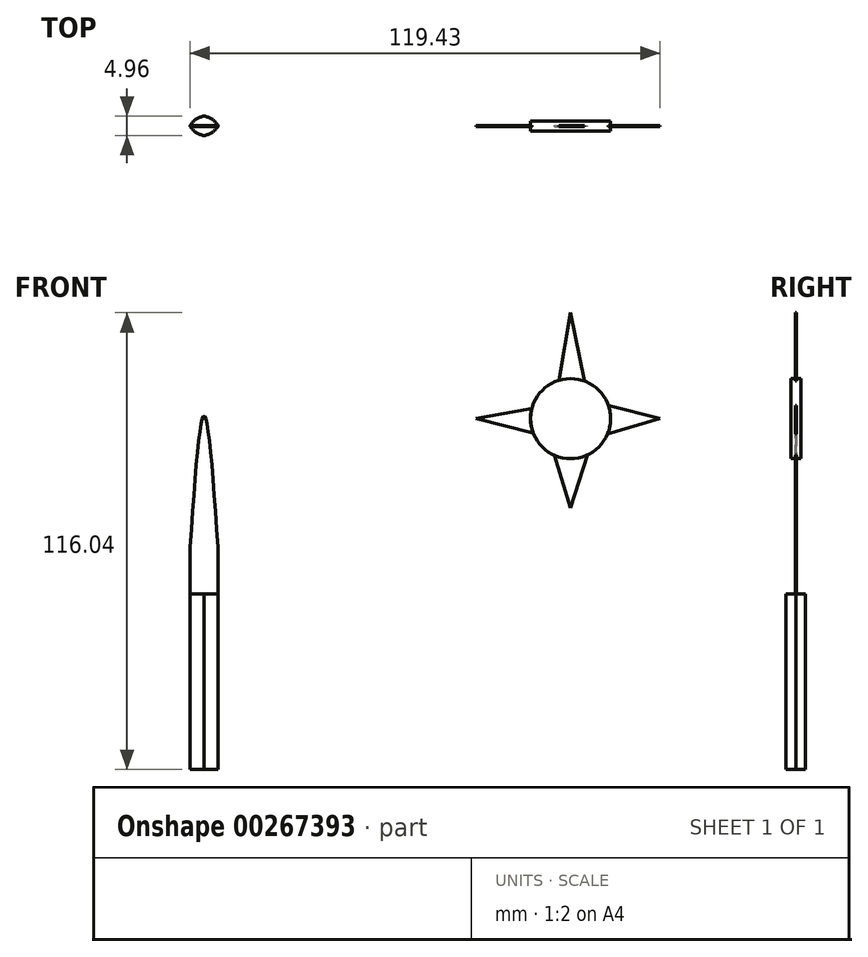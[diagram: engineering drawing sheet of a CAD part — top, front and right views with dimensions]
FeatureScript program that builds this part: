
annotation { "Feature Type Name" : "Feature", "Feature Type Description" : "" }
export const myFeature = defineFeature(function(context is Context, id is Id, definition is map)
    precondition{}
    {
        {
            var Q0;
            Q0=qCreatedBy(makeId("Front.planeOp"),FACE);
            var sketch = newSketch(context, id + "F0", { "sketchPlane" : qUnion([Q0])});
            skLineSegment(sketch, "E0.bottom", {"start": v(-61.66, -49.15) * mm, "end": v(-53.12, -49.15) * mm});
            skLineSegment(sketch, "E0.top", {"start": v(-61.66, -4.58) * mm, "end": v(-53.12, -4.58) * mm});
            skLineSegment(sketch, "E0.left", {"start": v(-61.66, -49.15) * mm, "end": v(-61.66, -4.58) * mm});
            skLineSegment(sketch, "E0.right", {"start": v(-53.12, -49.15) * mm, "end": v(-53.12, -4.58) * mm});
            skPoint(sketch, "E1.1.internal.snap0", {"position": v(-57.4, -4.58) * mm});
            skFitSpline(sketch, "E1", {"points": [v(-61.66, -4.58) * mm, v(-57.4, 40.6) * mm, v(-53.12, -4.58) * mm], "startDerivative": vector(8.55, 135.54) * mm, "endDerivative": vector(8.55, -135.54) * mm});
            skLineSegment(sketch, "E2", {"start": v(-61.66, -4.58) * mm, "end": v(-53.12, -8.83) * mm});
            skLineSegment(sketch, "E3", {"start": v(-53.12, -8.83) * mm, "end": v(-61.66, -12.87) * mm});
            skLineSegment(sketch, "E4", {"start": v(-61.66, -12.87) * mm, "end": v(-53.12, -15.68) * mm});
            skLineSegment(sketch, "E5", {"start": v(-53.12, -15.68) * mm, "end": v(-61.66, -19.7) * mm});
            skLineSegment(sketch, "E6", {"start": v(-61.66, -19.7) * mm, "end": v(-53.12, -23.53) * mm});
            skLineSegment(sketch, "E7", {"start": v(-53.12, -23.53) * mm, "end": v(-61.66, -27.49) * mm});
            skLineSegment(sketch, "E8", {"start": v(-61.66, -27.49) * mm, "end": v(-53.12, -31.45) * mm});
            skLineSegment(sketch, "E9", {"start": v(-53.12, -31.45) * mm, "end": v(-61.66, -37.05) * mm});
            skLineSegment(sketch, "E10", {"start": v(-61.66, -37.05) * mm, "end": v(-53.12, -41.01) * mm});
            skLineSegment(sketch, "E11", {"start": v(-53.12, -41.01) * mm, "end": v(-61.66, -44.67) * mm});
            skLineSegment(sketch, "E12", {"start": v(-61.66, -44.67) * mm, "end": v(-53.12, -49.15) * mm});
            skSolve(sketch);
        }
        {
            var Q0;
            Q0=makeQuery(id+"F0.imprint","IMPRINT",FACE,{"disambiguationData":[TD([[makeQuery(id+"F0.imprint","IMPRINT",EDGE,{"derivedFrom":sQuery(id+"F0.wireOp",EDGE,"E0.top")}),1.0]])]});
            extrude(context, id + "F1", {"entities" : qUnion([Q0]), "endBound" : BoundingType.SYMMETRIC, "depth" : 0.25 * mm});
        }
        {
            var Q0;
            {var subQ0=sQuery(id+"F0.wireOp",EDGE,"E0.top");Q0=makeQuery(id+"F0.imprint","IMPRINT",FACE,{"disambiguationData":[TD([[makeQuery(id+"F0.imprint","IMPRINT",EDGE,{"derivedFrom":subQ0}),-1.0]])]});}
            var Q1;
            {var subQ0=sQuery(id+"F0.wireOp",EDGE,"E2");Q1=makeQuery(id+"F0.imprint","IMPRINT",FACE,{"disambiguationData":[TD([[makeQuery(id+"F0.imprint","IMPRINT",EDGE,{"derivedFrom":subQ0}),-1.0]])]});}
            var Q2;
            {var subQ0=sQuery(id+"F0.wireOp",EDGE,"E3");Q2=makeQuery(id+"F0.imprint","IMPRINT",FACE,{"disambiguationData":[TD([[makeQuery(id+"F0.imprint","IMPRINT",EDGE,{"derivedFrom":subQ0}),1.0]])]});}
            var Q3;
            {var subQ0=sQuery(id+"F0.wireOp",EDGE,"E4");Q3=makeQuery(id+"F0.imprint","IMPRINT",FACE,{"disambiguationData":[TD([[makeQuery(id+"F0.imprint","IMPRINT",EDGE,{"derivedFrom":subQ0}),-1.0]])]});}
            var Q4;
            {var subQ0=sQuery(id+"F0.wireOp",EDGE,"E5");Q4=makeQuery(id+"F0.imprint","IMPRINT",FACE,{"disambiguationData":[TD([[makeQuery(id+"F0.imprint","IMPRINT",EDGE,{"derivedFrom":subQ0}),1.0]])]});}
            var Q5;
            {var subQ0=sQuery(id+"F0.wireOp",EDGE,"E6");Q5=makeQuery(id+"F0.imprint","IMPRINT",FACE,{"disambiguationData":[TD([[makeQuery(id+"F0.imprint","IMPRINT",EDGE,{"derivedFrom":subQ0}),-1.0]])]});}
            var Q6;
            {var subQ0=sQuery(id+"F0.wireOp",EDGE,"E7");Q6=makeQuery(id+"F0.imprint","IMPRINT",FACE,{"disambiguationData":[TD([[makeQuery(id+"F0.imprint","IMPRINT",EDGE,{"derivedFrom":subQ0}),1.0]])]});}
            var Q7;
            {var subQ0=sQuery(id+"F0.wireOp",EDGE,"E8");Q7=makeQuery(id+"F0.imprint","IMPRINT",FACE,{"disambiguationData":[TD([[makeQuery(id+"F0.imprint","IMPRINT",EDGE,{"derivedFrom":subQ0}),-1.0]])]});}
            var Q8;
            {var subQ0=sQuery(id+"F0.wireOp",EDGE,"E9");Q8=makeQuery(id+"F0.imprint","IMPRINT",FACE,{"disambiguationData":[TD([[makeQuery(id+"F0.imprint","IMPRINT",EDGE,{"derivedFrom":subQ0}),1.0]])]});}
            var Q9;
            {var subQ0=sQuery(id+"F0.wireOp",EDGE,"E10");Q9=makeQuery(id+"F0.imprint","IMPRINT",FACE,{"disambiguationData":[TD([[makeQuery(id+"F0.imprint","IMPRINT",EDGE,{"derivedFrom":subQ0}),-1.0]])]});}
            var Q10;
            {var subQ2=sQuery(id+"F0.wireOp",EDGE,"E11");Q10=makeQuery(id+"F0.imprint","IMPRINT",FACE,{"disambiguationData":[TD([[makeQuery(id+"F0.imprint","IMPRINT",EDGE,{"derivedFrom":subQ2}),1.0]])]});}
            var Q11;
            {var subQ0=sQuery(id+"F0.wireOp",EDGE,"E0.bottom");Q11=makeQuery(id+"F0.imprint","IMPRINT",FACE,{"disambiguationData":[TD([[makeQuery(id+"F0.imprint","IMPRINT",EDGE,{"derivedFrom":subQ0}),1.0]])]});}
            extrude(context, id + "F2", {"entities" : qUnion([Q0, Q1, Q2, Q3, Q4, Q5, Q6, Q7, Q8, Q9, Q10, Q11]), "operationType" : NewBodyOperationType.ADD, "endBound" : BoundingType.SYMMETRIC, "depth" : 5.08 * mm});
        }
        {
            var Q0;
            Q0=makeQuery(id+"F2.opExtrude","CAP_EDGE",EDGE,{"disambiguationData":[OSD([sQuery(id+"F0.wireOp",EDGE,"E0.left")])],"isStart":true});
            var Q1;
            Q1=makeQuery(id+"F2.opExtrude","CAP_EDGE",EDGE,{"disambiguationData":[OSD([sQuery(id+"F0.wireOp",EDGE,"E0.left")])],"isStart":false});
            var Q2;
            Q2=makeQuery(id+"F2.opExtrude","CAP_EDGE",EDGE,{"disambiguationData":[OSD([sQuery(id+"F0.wireOp",EDGE,"E0.right")])],"isStart":false});
            var Q3;
            Q3=makeQuery(id+"F2.opExtrude","CAP_EDGE",EDGE,{"disambiguationData":[OSD([sQuery(id+"F0.wireOp",EDGE,"E0.right")])],"isStart":true});
            fillet(context, id + "F3", {"entities" : qUnion([Q0, Q1, Q2, Q3]), "radius" : 5.08 * mm, "tangentPropagation" : true, "allowEdgeOverflow" : false});
        }
        {
            var Q0;
            Q0=qCreatedBy(makeId("Front.planeOp"),FACE);
            var sketch = newSketch(context, id + "F4", { "sketchPlane" : qUnion([Q0])});
            skCircle(sketch, "E13", {"center": v(35.72, 40) * mm, "radius": 10.17 * mm});
            skLineSegment(sketch, "E14", {"start": v(11.67, 40) * mm, "end": v(25.87, 42.54) * mm});
            skLineSegment(sketch, "E15", {"start": v(11.67, 40) * mm, "end": v(26.22, 36.35) * mm});
            skLineSegment(sketch, "E16", {"start": v(35.72, 17.32) * mm, "end": v(39.99, 30.77) * mm});
            skLineSegment(sketch, "E17", {"start": v(35.72, 17.32) * mm, "end": v(31.67, 30.66) * mm});
            skLineSegment(sketch, "E18", {"start": v(58.45, 40) * mm, "end": v(45.1, 36.09) * mm});
            skLineSegment(sketch, "E19", {"start": v(58.45, 40) * mm, "end": v(45.34, 43.26) * mm});
            skLineSegment(sketch, "E20", {"start": v(35.72, 66.89) * mm, "end": v(39.3, 49.5) * mm});
            skLineSegment(sketch, "E21", {"start": v(35.72, 66.89) * mm, "end": v(32.79, 49.72) * mm});
            skSolve(sketch);
        }
        {
            var Q0;
            {var subQ0=sQuery(id+"F4.wireOp",EDGE,"E13");var subQ5=makeQuery(id+"F4.imprint","INTERSECT",VERTEX,{"derivedFrom":[subQ0,sQuery(id+"F4.wireOp",EDGE,"E19")]});Q0=makeQuery(id+"F4.imprint","IMPRINT",FACE,{"disambiguationData":[TD([[makeQuery(id+"F4.imprint","IMPRINT",EDGE,{"disambiguationData":[TD([[subQ5,-1.0]])],"derivedFrom":subQ0}),1.0]])]});}
            extrude(context, id + "F5", {"entities" : qUnion([Q0]), "endBound" : BoundingType.SYMMETRIC, "depth" : 2.54 * mm});
        }
        {
            var Q0;
            {var subQ0=sQuery(id+"F4.wireOp",EDGE,"E14");Q0=makeQuery(id+"F4.imprint","IMPRINT",FACE,{"disambiguationData":[TD([[makeQuery(id+"F4.imprint","IMPRINT",EDGE,{"derivedFrom":subQ0}),-1.0]])]});}
            var Q1;
            {var subQ0=sQuery(id+"F4.wireOp",EDGE,"E20");Q1=makeQuery(id+"F4.imprint","IMPRINT",FACE,{"disambiguationData":[TD([[makeQuery(id+"F4.imprint","IMPRINT",EDGE,{"derivedFrom":subQ0}),-1.0]])]});}
            var Q2;
            {var subQ0=sQuery(id+"F4.wireOp",EDGE,"E16");Q2=makeQuery(id+"F4.imprint","IMPRINT",FACE,{"disambiguationData":[TD([[makeQuery(id+"F4.imprint","IMPRINT",EDGE,{"derivedFrom":subQ0}),1.0]])]});}
            var Q3;
            {var subQ0=sQuery(id+"F4.wireOp",EDGE,"E18");Q3=makeQuery(id+"F4.imprint","IMPRINT",FACE,{"disambiguationData":[TD([[makeQuery(id+"F4.imprint","IMPRINT",EDGE,{"derivedFrom":subQ0}),-1.0]])]});}
            extrude(context, id + "F6", {"entities" : qUnion([Q0, Q1, Q2, Q3]), "operationType" : NewBodyOperationType.ADD, "endBound" : BoundingType.SYMMETRIC, "depth" : 0.25 * mm});
        }
    });
